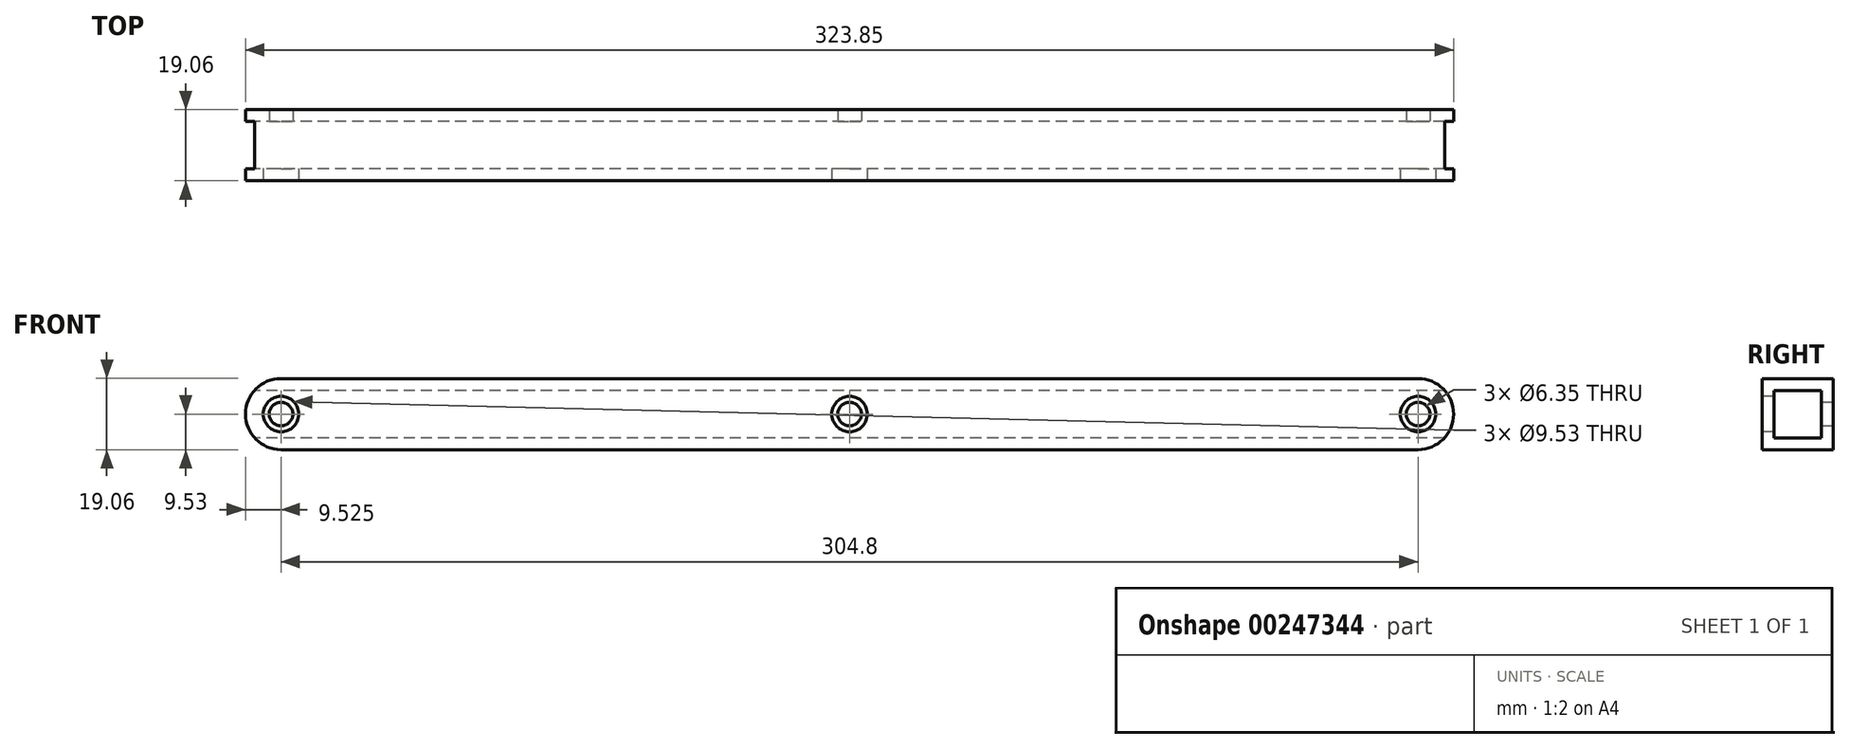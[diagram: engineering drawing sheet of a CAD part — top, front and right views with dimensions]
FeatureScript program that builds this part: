
annotation { "Feature Type Name" : "Feature", "Feature Type Description" : "" }
export const myFeature = defineFeature(function(context is Context, id is Id, definition is map)
    precondition{}
    {
        {
            var Q0;
            Q0=qCreatedBy(makeId("Right.planeOp"),FACE);
            var sketch = newSketch(context, id + "F0", { "sketchPlane" : qUnion([Q0])});
            skLineSegment(sketch, "E0.bottom", {"start": v(6.35, 6.35) * mm, "end": v(-6.35, 6.35) * mm});
            skLineSegment(sketch, "E0.top", {"start": v(6.35, -6.35) * mm, "end": v(-6.35, -6.35) * mm});
            skLineSegment(sketch, "E0.left", {"start": v(6.35, 6.35) * mm, "end": v(6.35, -6.35) * mm});
            skLineSegment(sketch, "E0.right", {"start": v(-6.35, 6.35) * mm, "end": v(-6.35, -6.35) * mm});
            skPoint(sketch, "E0.middle", {"position": v(0, 0) * mm});
            skLineSegment(sketch, "E1.bottom", {"start": v(9.53, 9.53) * mm, "end": v(-9.53, 9.53) * mm});
            skLineSegment(sketch, "E1.top", {"start": v(9.53, -9.53) * mm, "end": v(-9.53, -9.53) * mm});
            skLineSegment(sketch, "E1.left", {"start": v(9.53, 9.53) * mm, "end": v(9.53, -9.53) * mm});
            skLineSegment(sketch, "E1.right", {"start": v(-9.53, 9.53) * mm, "end": v(-9.53, -9.53) * mm});
            skSolve(sketch);
        }
        {
            var Q0;
            Q0=makeQuery(id+"F0.imprint","IMPRINT",FACE,{"disambiguationData":[TD([[makeQuery(id+"F0.imprint","IMPRINT",EDGE,{"derivedFrom":sQuery(id+"F0.wireOp",EDGE,"E0.bottom")}),-1.0]])]});
            extrude(context, id + "F1", {"entities" : qUnion([Q0]), "depth" : 323.85 * mm});
        }
        {
            var Q0;
            Q0=makeQuery(id+"F1.opExtrude","SWEPT_FACE",FACE,{"disambiguationData":[OSD([sQuery(id+"F0.wireOp",EDGE,"E1.right")])]});
            var sketch = newSketch(context, id + "F2", { "sketchPlane" : qUnion([Q0])});
            skLineSegment(sketch, "E2", {"start": v(161.93, 9.53) * mm, "end": v(161.93, -9.53) * mm, "construction": true});
            skLineSegment(sketch, "E3", {"start": v(0, 0) * mm, "end": v(9.53, 0) * mm, "construction": true});
            skPoint(sketch, "E3.endSnap0", {"position": v(0, 0) * mm});
            skLineSegment(sketch, "E4", {"start": v(323.85, 0) * mm, "end": v(314.33, 0) * mm, "construction": true});
            skPoint(sketch, "E4.endSnap0", {"position": v(323.85, 0) * mm});
            skCircle(sketch, "E5", {"center": v(9.53, 0) * mm, "radius": 4.76 * mm});
            skCircle(sketch, "E6", {"center": v(161.93, 0) * mm, "radius": 4.76 * mm});
            skCircle(sketch, "E7", {"center": v(314.33, 0) * mm, "radius": 4.76 * mm});
            skCircle(sketch, "E8", {"center": v(9.53, 0) * mm, "radius": 3.18 * mm});
            skCircle(sketch, "E9", {"center": v(161.93, 0) * mm, "radius": 3.18 * mm});
            skCircle(sketch, "E10", {"center": v(314.33, 0) * mm, "radius": 3.18 * mm});
            skSolve(sketch);
        }
        {
            var Q0;
            Q0=makeQuery(id+"F1.opExtrude","CAP_EDGE",EDGE,{"disambiguationData":[OSD([sQuery(id+"F0.wireOp",EDGE,"E1.bottom")])],"isStart":true});
            var Q1;
            Q1=makeQuery(id+"F1.opExtrude","CAP_EDGE",EDGE,{"disambiguationData":[OSD([sQuery(id+"F0.wireOp",EDGE,"E1.top")])],"isStart":true});
            fillet(context, id + "F3", {"entities" : qUnion([Q0, Q1]), "radius" : 9.52 * mm, "tangentPropagation" : true, "allowEdgeOverflow" : false});
        }
        {
            var Q0;
            Q0=makeQuery(id+"F1.opExtrude","CAP_EDGE",EDGE,{"disambiguationData":[OSD([sQuery(id+"F0.wireOp",EDGE,"E1.bottom")])],"isStart":false});
            var Q1;
            Q1=makeQuery(id+"F1.opExtrude","CAP_EDGE",EDGE,{"disambiguationData":[OSD([sQuery(id+"F0.wireOp",EDGE,"E1.top")])],"isStart":false});
            fillet(context, id + "F4", {"entities" : qUnion([Q0, Q1]), "radius" : 9.52 * mm, "tangentPropagation" : true, "allowEdgeOverflow" : false});
        }
        {
            var Q0;
            Q0=makeQuery(id+"F2.imprint","IMPRINT",FACE,{"disambiguationData":[TD([[makeQuery(id+"F2.imprint","IMPRINT",EDGE,{"derivedFrom":sQuery(id+"F2.wireOp",EDGE,"E10")}),1.0]])]});
            var Q1;
            Q1=makeQuery(id+"F2.imprint","IMPRINT",FACE,{"disambiguationData":[TD([[makeQuery(id+"F2.imprint","IMPRINT",EDGE,{"derivedFrom":sQuery(id+"F2.wireOp",EDGE,"E9")}),1.0]])]});
            var Q2;
            Q2=makeQuery(id+"F2.imprint","IMPRINT",FACE,{"disambiguationData":[TD([[makeQuery(id+"F2.imprint","IMPRINT",EDGE,{"derivedFrom":sQuery(id+"F2.wireOp",EDGE,"E8")}),1.0]])]});
            var Q3;
            Q3=sQuery(id+"F2.wireOp",EDGE,"E8");
            var Q4;
            Q4=sQuery(id+"F2.wireOp",EDGE,"E9");
            var Q5;
            Q5=sQuery(id+"F2.wireOp",EDGE,"E10");
            extrude(context, id + "F5", {"entities" : qUnion([Q0, Q1, Q2]), "operationType" : NewBodyOperationType.REMOVE, "surfaceEntities" : qUnion([Q3, Q4, Q5]), "endBound" : BoundingType.THROUGH_ALL, "oppositeDirection" : true, "depth" : 25.4 * mm});
        }
        {
            var Q0;
            Q0=makeQuery(id+"F2.imprint","IMPRINT",FACE,{"disambiguationData":[TD([[makeQuery(id+"F2.imprint","IMPRINT",EDGE,{"derivedFrom":sQuery(id+"F2.wireOp",EDGE,"E5")}),1.0]])]});
            var Q1;
            Q1=makeQuery(id+"F2.imprint","IMPRINT",FACE,{"disambiguationData":[TD([[makeQuery(id+"F2.imprint","IMPRINT",EDGE,{"derivedFrom":sQuery(id+"F2.wireOp",EDGE,"E6")}),1.0]])]});
            var Q2;
            Q2=makeQuery(id+"F2.imprint","IMPRINT",FACE,{"disambiguationData":[TD([[makeQuery(id+"F2.imprint","IMPRINT",EDGE,{"derivedFrom":sQuery(id+"F2.wireOp",EDGE,"E7")}),1.0]])]});
            extrude(context, id + "F6", {"entities" : qUnion([Q0, Q1, Q2]), "operationType" : NewBodyOperationType.REMOVE, "endBound" : BoundingType.UP_TO_NEXT, "oppositeDirection" : true, "depth" : 25.4 * mm});
        }
    });
